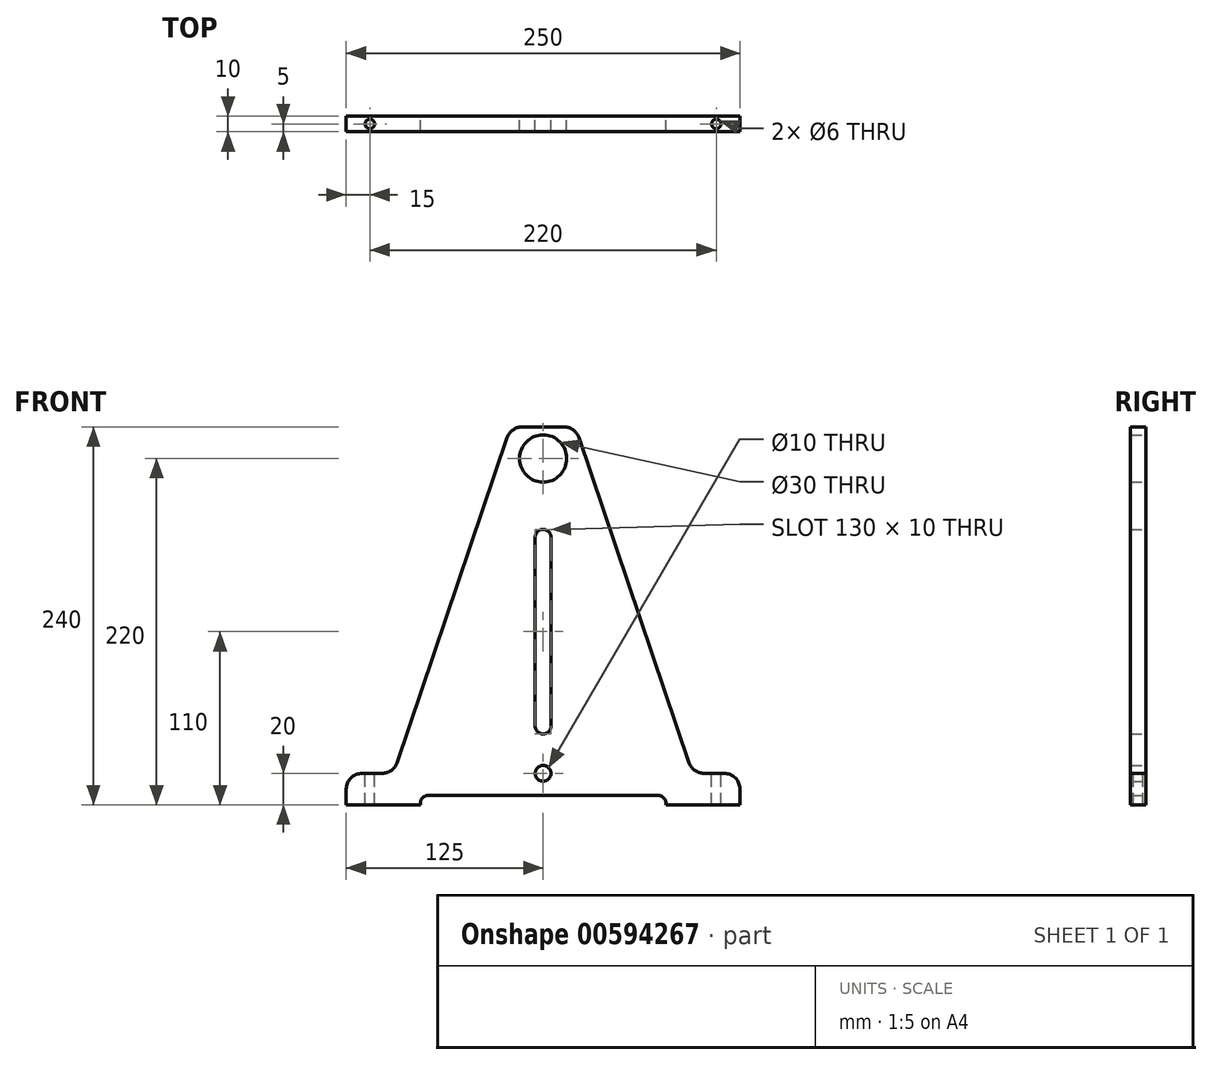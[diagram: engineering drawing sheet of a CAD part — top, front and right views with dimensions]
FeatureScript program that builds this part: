
annotation { "Feature Type Name" : "Feature", "Feature Type Description" : "" }
export const myFeature = defineFeature(function(context is Context, id is Id, definition is map)
    precondition{}
    {
        {
            var Q0;
            Q0=qCreatedBy(makeId("Front.planeOp"),FACE);
            var sketch = newSketch(context, id + "F0", { "sketchPlane" : qUnion([Q0])});
            skLineSegment(sketch, "E0", {"start": v(-102.17, 0) * mm, "end": v(-115, 0) * mm, "construction": true});
            skLineSegment(sketch, "E1", {"start": v(0, 0) * mm, "end": v(0, 200) * mm, "construction": true});
            skLineSegment(sketch, "E2", {"start": v(0, 200) * mm, "end": v(-30, 200) * mm, "construction": true});
            skCircle(sketch, "E3", {"center": v(0, 0) * mm, "radius": 5 * mm});
            skCircle(sketch, "E4", {"center": v(0, 200) * mm, "radius": 15 * mm});
            skLineSegment(sketch, "E5", {"start": v(-125, -20) * mm, "end": v(-125, -10) * mm});
            skLineSegment(sketch, "E6.0", {"start": v(0, 220) * mm, "end": v(-13.35, 220) * mm});
            skLineSegment(sketch, "E7", {"start": v(-125, 0) * mm, "end": v(-95, 0) * mm});
            skLineSegment(sketch, "E8", {"start": v(-92.7, 6.8) * mm, "end": v(-22.82, 213.2) * mm});
            skLineSegment(sketch, "E9.MirrorCS", {"start": v(125, -20) * mm, "end": v(125, -10) * mm});
            skLineSegment(sketch, "E10.MirrorCS", {"start": v(115, 0) * mm, "end": v(102.17, 0) * mm});
            skLineSegment(sketch, "E11.MirrorCS", {"start": v(92.7, 6.8) * mm, "end": v(22.82, 213.2) * mm});
            skLineSegment(sketch, "E12.MirrorCS", {"start": v(0, 220) * mm, "end": v(13.35, 220) * mm});
            skPoint(sketch, "E13.orphan", {"position": v(0, -20) * mm});
            skLineSegment(sketch, "E14", {"start": v(0, -20) * mm, "end": v(0, -14) * mm, "construction": true});
            skLineSegment(sketch, "E15.0", {"start": v(-78, -20) * mm, "end": v(-78, -19) * mm});
            skLineSegment(sketch, "E16.MirrorCS", {"start": v(78, -20) * mm, "end": v(78, -19) * mm});
            skLineSegment(sketch, "E17", {"start": v(-125, -20) * mm, "end": v(-78, -20) * mm});
            skLineSegment(sketch, "E18", {"start": v(-73, -14) * mm, "end": v(73, -14) * mm});
            skLineSegment(sketch, "E19", {"start": v(78, -20) * mm, "end": v(125, -20) * mm});
            skPoint(sketch, "E20.visualSharp", {"position": v(-78, -14) * mm});
            skArc(sketch, "E20.filletArc", {"start": v(-73, -14) * mm, "mid": v(-76.54, -15.46) * mm, "end": v(-78, -19) * mm});
            skPoint(sketch, "E21.visualSharp", {"position": v(78, -14) * mm});
            skArc(sketch, "E21.filletArc", {"start": v(78, -19) * mm, "mid": v(76.54, -15.46) * mm, "end": v(73, -14) * mm});
            skArc(sketch, "E22", {"start": v(5, 150) * mm, "mid": v(0, 155) * mm, "end": v(-5, 150) * mm});
            skArc(sketch, "E23", {"start": v(-5, 30) * mm, "mid": v(0, 25) * mm, "end": v(5, 30) * mm});
            skLineSegment(sketch, "E24", {"start": v(-5, 30) * mm, "end": v(-5, 150) * mm});
            skLineSegment(sketch, "E25.MirrorCS", {"start": v(5, 30) * mm, "end": v(5, 150) * mm});
            skPoint(sketch, "E26.visualSharp", {"position": v(-125, 0) * mm});
            skArc(sketch, "E26.filletArc", {"start": v(-115, 0) * mm, "mid": v(-122.07, -2.93) * mm, "end": v(-125, -10) * mm});
            skPoint(sketch, "E27.newPointB", {"position": v(-95, 0) * mm});
            skArc(sketch, "E27.filletArc", {"start": v(-102.17, 0) * mm, "mid": v(-96.34, 1.87) * mm, "end": v(-92.7, 6.8) * mm});
            skPoint(sketch, "E28.visualSharp", {"position": v(-20.52, 220) * mm});
            skArc(sketch, "E28.filletArc", {"start": v(-13.35, 220) * mm, "mid": v(-19.18, 218.13) * mm, "end": v(-22.82, 213.2) * mm});
            skPoint(sketch, "E29.visualSharp", {"position": v(20.52, 220) * mm});
            skArc(sketch, "E29.filletArc", {"start": v(22.82, 213.2) * mm, "mid": v(19.18, 218.13) * mm, "end": v(13.35, 220) * mm});
            skPoint(sketch, "E30.visualSharp", {"position": v(95, 0) * mm});
            skArc(sketch, "E30.filletArc", {"start": v(92.7, 6.8) * mm, "mid": v(96.34, 1.87) * mm, "end": v(102.17, 0) * mm});
            skPoint(sketch, "E31.visualSharp", {"position": v(125, 0) * mm});
            skArc(sketch, "E31.filletArc", {"start": v(125, -10) * mm, "mid": v(122.07, -2.93) * mm, "end": v(115, 0) * mm});
            skSolve(sketch);
        }
        {
            var Q0;
            Q0=makeQuery(id+"F0.imprint","IMPRINT",FACE,{"disambiguationData":[TD([[makeQuery(id+"F0.imprint","IMPRINT",EDGE,{"derivedFrom":sQuery(id+"F0.wireOp",EDGE,"E3")}),-1.0]])]});
            extrude(context, id + "F1", {"entities" : qUnion([Q0]), "depth" : 10 * mm, "offsetDistance" : 25 * mm});
        }
        {
            var Q0;
            Q0=makeQuery(id+"F1.opExtrude","SWEPT_FACE",FACE,{"disambiguationData":[OSD([sQuery(id+"F0.wireOp",EDGE,"E7")])]});
            var sketch = newSketch(context, id + "F2", { "sketchPlane" : qUnion([Q0])});
            skPoint(sketch, "E32", {"position": v(-110, -5) * mm});
            skPoint(sketch, "E32.positionSnap0", {"position": v(-125, -5) * mm});
            skPoint(sketch, "E33", {"position": v(110, -5) * mm});
            skSolve(sketch);
        }
        {
            var Q0;
            Q0=sQuery(id+"F2.wireOp",VERTEX,"E32");
            var Q1;
            Q1=sQuery(id+"F2.wireOp",VERTEX,"E33");
            var Q2;
            Q2=makeQuery(id+"F1.opExtrude","SWEPT_BODY",BODY,{"disambiguationData":[OSD([sQuery(id+"F0.wireOp",EDGE,"E3"),sQuery(id+"F0.wireOp",EDGE,"E4"),sQuery(id+"F0.wireOp",EDGE,"E5"),sQuery(id+"F0.wireOp",EDGE,"E6.0"),sQuery(id+"F0.wireOp",EDGE,"E7"),sQuery(id+"F0.wireOp",EDGE,"E8"),sQuery(id+"F0.wireOp",EDGE,"E9.MirrorCS"),sQuery(id+"F0.wireOp",EDGE,"E10.MirrorCS"),sQuery(id+"F0.wireOp",EDGE,"E11.MirrorCS"),sQuery(id+"F0.wireOp",EDGE,"E12.MirrorCS"),sQuery(id+"F0.wireOp",EDGE,"E15.0"),sQuery(id+"F0.wireOp",EDGE,"E16.MirrorCS"),sQuery(id+"F0.wireOp",EDGE,"E17"),sQuery(id+"F0.wireOp",EDGE,"E18"),sQuery(id+"F0.wireOp",EDGE,"E19"),sQuery(id+"F0.wireOp",EDGE,"E20.filletArc"),sQuery(id+"F0.wireOp",EDGE,"E21.filletArc"),sQuery(id+"F0.wireOp",EDGE,"E22"),sQuery(id+"F0.wireOp",EDGE,"E23"),sQuery(id+"F0.wireOp",EDGE,"E24"),sQuery(id+"F0.wireOp",EDGE,"E25.MirrorCS")])]});
            hole(context, id + "F3", {"style" : HoleStyle.SIMPLE, "endStyle" : HoleEndStyle.THROUGH, "holeDiameter" : 6 * mm, "majorDiameter" : 5 * mm, "isTappedThrough" : true, "tappedDepth" : 12 * mm, "tapClearance" : 3, "locations" : qUnion([Q0, Q1]), "scope" : qUnion([Q2])});
        }
    });
